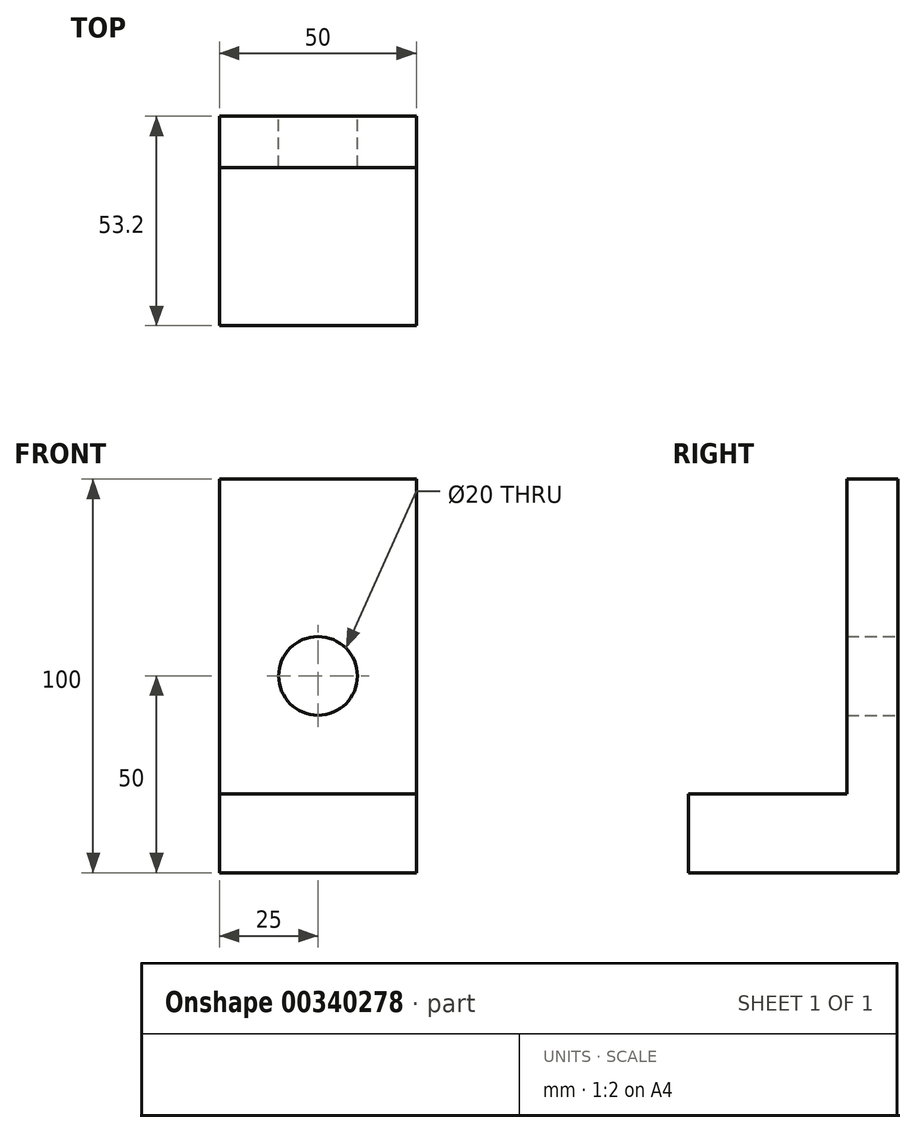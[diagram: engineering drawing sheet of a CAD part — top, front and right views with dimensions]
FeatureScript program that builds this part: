
annotation { "Feature Type Name" : "Feature", "Feature Type Description" : "" }
export const myFeature = defineFeature(function(context is Context, id is Id, definition is map)
    precondition{}
    {
        {
            var Q0;
            Q0=qCreatedBy(makeId("Front.planeOp"),FACE);
            var sketch = newSketch(context, id + "F0", { "sketchPlane" : qUnion([Q0])});
            skLineSegment(sketch, "E0.bottom", {"start": v(25, -50) * mm, "end": v(-25, -50) * mm});
            skLineSegment(sketch, "E0.top", {"start": v(25, 50) * mm, "end": v(-25, 50) * mm});
            skLineSegment(sketch, "E0.left", {"start": v(25, -50) * mm, "end": v(25, 50) * mm});
            skLineSegment(sketch, "E0.right", {"start": v(-25, -50) * mm, "end": v(-25, 50) * mm});
            skPoint(sketch, "E0.middle", {"position": v(0, 0) * mm});
            skLineSegment(sketch, "E1.bottom", {"start": v(-25, -50) * mm, "end": v(-25, -50) * mm});
            skLineSegment(sketch, "E1.top", {"start": v(-25, 50) * mm, "end": v(-25, 50) * mm});
            skPoint(sketch, "E1.middle", {"position": v(-25, 0) * mm});
            skSolve(sketch);
        }
        {
            var Q0;
            Q0=makeQuery(id+"F0.imprint","IMPRINT",FACE,{"disambiguationData":[TD([[makeQuery(id+"F0.imprint","IMPRINT",EDGE,{"derivedFrom":sQuery(id+"F0.wireOp",EDGE,"E0.bottom")}),-1.0]])]});
            extrude(context, id + "F1", {"entities" : qUnion([Q0]), "depth" : 13 * mm});
        }
        {
            var Q0;
            Q0=makeQuery(id+"F1.opExtrude","CAP_FACE",FACE,{"disambiguationData":[OSD([sQuery(id+"F0.wireOp",EDGE,"E0.bottom"),sQuery(id+"F0.wireOp",EDGE,"E0.top"),sQuery(id+"F0.wireOp",EDGE,"E0.left"),sQuery(id+"F0.wireOp",EDGE,"E0.right")])],"isStart":false});
            var sketch = newSketch(context, id + "F2", { "sketchPlane" : qUnion([Q0])});
            skLineSegment(sketch, "E2.bottom", {"start": v(-25, -50) * mm, "end": v(25, -50) * mm});
            skLineSegment(sketch, "E2.top", {"start": v(-25, -30) * mm, "end": v(25, -30) * mm});
            skLineSegment(sketch, "E2.left", {"start": v(-25, -50) * mm, "end": v(-25, -30) * mm});
            skLineSegment(sketch, "E2.right", {"start": v(25, -50) * mm, "end": v(25, -30) * mm});
            skSolve(sketch);
        }
        {
            var Q0;
            Q0=makeQuery(id+"F2.imprint","IMPRINT",FACE,{"disambiguationData":[TD([[makeQuery(id+"F2.imprint","IMPRINT",EDGE,{"derivedFrom":sQuery(id+"F2.wireOp",EDGE,"E2.bottom")}),-1.0]])]});
            var Q1;
            Q1=makeQuery(id+"F2.imprint","IMPRINT",FACE,{"disambiguationData":[TD([[makeQuery(id+"F2.imprint","IMPRINT",EDGE,{"derivedFrom":sQuery(id+"F2.wireOp",EDGE,"Z7Jv5Qa4-uOAK-FNjj-ulDm-aVwysjf45ypk")}),1.0]])]});
            extrude(context, id + "F3", {"entities" : qUnion([Q0, Q1]), "operationType" : NewBodyOperationType.ADD, "depth" : 40.2 * mm});
        }
        {
            var Q0;
            Q0=makeQuery(id+"F1.opExtrude","CAP_FACE",FACE,{"disambiguationData":[OSD([sQuery(id+"F0.wireOp",EDGE,"E0.bottom"),sQuery(id+"F0.wireOp",EDGE,"E0.top"),sQuery(id+"F0.wireOp",EDGE,"E0.left"),sQuery(id+"F0.wireOp",EDGE,"E0.right")])],"isStart":true});
            var sketch = newSketch(context, id + "F4", { "sketchPlane" : qUnion([Q0])});
            skCircle(sketch, "E3", {"center": v(0, 0) * mm, "radius": 10 * mm});
            skSolve(sketch);
        }
        {
            var Q0;
            Q0=makeQuery(id+"F4.imprint","IMPRINT",FACE,{"disambiguationData":[TD([[makeQuery(id+"F4.imprint","IMPRINT",EDGE,{"derivedFrom":sQuery(id+"F4.wireOp",EDGE,"E3")}),1.0]])]});
            extrude(context, id + "F5", {"entities" : qUnion([Q0]), "operationType" : NewBodyOperationType.REMOVE, "oppositeDirection" : true, "depth" : 66.4 * mm});
        }
    });
